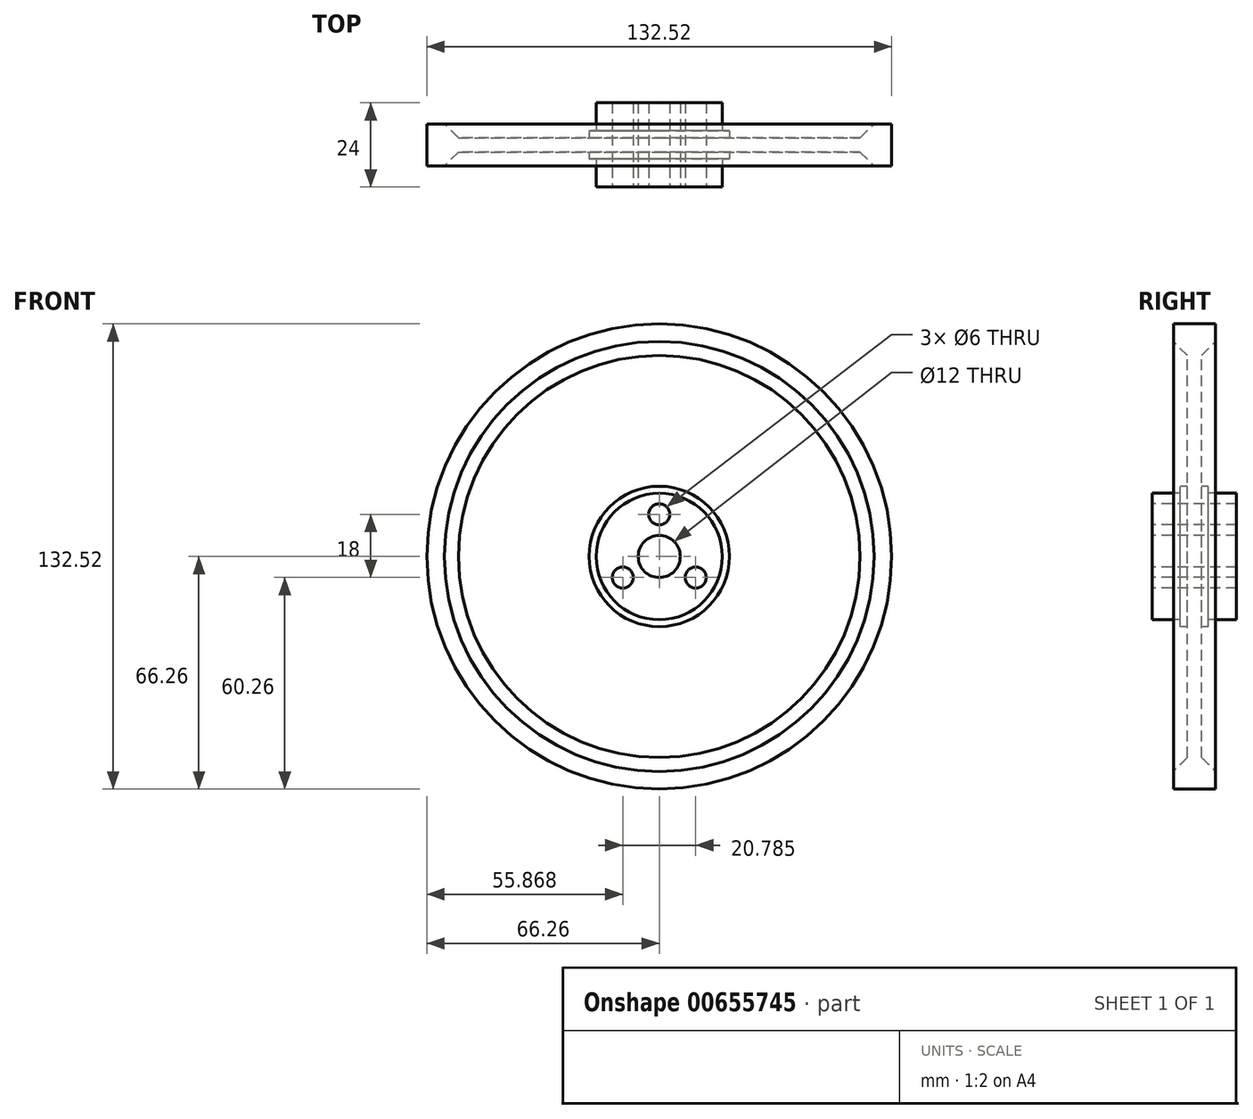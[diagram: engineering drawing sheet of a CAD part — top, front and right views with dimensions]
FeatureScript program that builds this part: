
annotation { "Feature Type Name" : "Feature", "Feature Type Description" : "" }
export const myFeature = defineFeature(function(context is Context, id is Id, definition is map)
    precondition{}
    {
        {
            var Q0;
            Q0=qCreatedBy(makeId("Right.planeOp"),FACE);
            var sketch = newSketch(context, id + "F0", { "sketchPlane" : qUnion([Q0])});
            skLineSegment(sketch, "E0", {"start": v(0, 66.25) * mm, "end": v(-6, 66.25) * mm});
            skLineSegment(sketch, "E1", {"start": v(-12, 18) * mm, "end": v(-12, 6) * mm});
            skLineSegment(sketch, "E2", {"start": v(-12, 6) * mm, "end": v(0, 6) * mm});
            skLineSegment(sketch, "E3", {"start": v(-80.76, 0) * mm, "end": v(80.56, 0) * mm, "construction": true});
            skLineSegment(sketch, "E4", {"start": v(-12, 12) * mm, "end": v(33.3, 12) * mm, "construction": true});
            skLineSegment(sketch, "E5", {"start": v(-12, 18) * mm, "end": v(-4, 18) * mm});
            skLineSegment(sketch, "E6", {"start": v(-4, 18) * mm, "end": v(-4, 20) * mm});
            skLineSegment(sketch, "E7", {"start": v(-4, 20) * mm, "end": v(-2, 20) * mm});
            skLineSegment(sketch, "E8", {"start": v(-6, 61.25) * mm, "end": v(-6, 66.25) * mm});
            skLineSegment(sketch, "E9", {"start": v(-6, 61.25) * mm, "end": v(-2, 57.26) * mm});
            skLineSegment(sketch, "E10", {"start": v(-2, 57.26) * mm, "end": v(-2, 20) * mm});
            skLineSegment(sketch, "E11", {"start": v(0, 66.25) * mm, "end": v(0, 6) * mm, "construction": true});
            skLineSegment(sketch, "E12.MirrorCS", {"start": v(0, 66.25) * mm, "end": v(6, 66.25) * mm});
            skLineSegment(sketch, "E13.MirrorCS", {"start": v(6, 61.25) * mm, "end": v(6, 66.25) * mm});
            skLineSegment(sketch, "E14.MirrorCS", {"start": v(6, 61.25) * mm, "end": v(2, 57.26) * mm});
            skLineSegment(sketch, "E15.MirrorCS", {"start": v(2, 57.26) * mm, "end": v(2, 20) * mm});
            skLineSegment(sketch, "E16.MirrorCS", {"start": v(4, 20) * mm, "end": v(2, 20) * mm});
            skLineSegment(sketch, "E17.MirrorCS", {"start": v(4, 18) * mm, "end": v(4, 20) * mm});
            skLineSegment(sketch, "E18.MirrorCS", {"start": v(12, 18) * mm, "end": v(4, 18) * mm});
            skLineSegment(sketch, "E19.MirrorCS", {"start": v(12, 18) * mm, "end": v(12, 6) * mm});
            skLineSegment(sketch, "E20.MirrorCS", {"start": v(12, 6) * mm, "end": v(0, 6) * mm});
            skSolve(sketch);
        }
        {
            var Q0;
            Q0 = qSketchRegion(id + "F0", true);
            var Q1;
            Q1=sQuery(id+"F0.wireOp",EDGE,"E3");
            revolve(context, id + "F1", {"entities" : qUnion([Q0]), "axis" : qUnion([Q1]), "revolveType" : RevolveType.FULL});
        }
        {
            var Q0;
            Q0=makeQuery(id+"F1.opRevolve","SWEPT_FACE",FACE,{"disambiguationData":[OSD([sQuery(id+"F0.wireOp",EDGE,"E1")])]});
            var sketch = newSketch(context, id + "F2", { "sketchPlane" : qUnion([Q0])});
            skPoint(sketch, "E21", {"position": v(0, 12) * mm});
            skPoint(sketch, "E22.1.0", {"position": v(-10.4, -6) * mm});
            skPoint(sketch, "E22.2.0", {"position": v(10.4, -6) * mm});
            skPoint(sketch, "E22.center", {"position": v(0, 0) * mm});
            skSolve(sketch);
        }
        {
            var Q0;
            Q0=sQuery(id+"F2.wireOp",VERTEX,"E21");
            var Q1;
            Q1=sQuery(id+"F2.wireOp",VERTEX,"E22.2.0");
            var Q2;
            Q2=sQuery(id+"F2.wireOp",VERTEX,"E22.1.0");
            var Q3;
            Q3=makeQuery(id+"F1.opRevolve","SWEPT_BODY",BODY,{"disambiguationData":[OSD([sQuery(id+"F0.wireOp",EDGE,"E0"),sQuery(id+"F0.wireOp",EDGE,"E1"),sQuery(id+"F0.wireOp",EDGE,"E2"),sQuery(id+"F0.wireOp",EDGE,"E5"),sQuery(id+"F0.wireOp",EDGE,"E6"),sQuery(id+"F0.wireOp",EDGE,"E7"),sQuery(id+"F0.wireOp",EDGE,"E8"),sQuery(id+"F0.wireOp",EDGE,"E9"),sQuery(id+"F0.wireOp",EDGE,"E10"),sQuery(id+"F0.wireOp",EDGE,"E12.MirrorCS"),sQuery(id+"F0.wireOp",EDGE,"E13.MirrorCS"),sQuery(id+"F0.wireOp",EDGE,"E14.MirrorCS"),sQuery(id+"F0.wireOp",EDGE,"E15.MirrorCS"),sQuery(id+"F0.wireOp",EDGE,"E16.MirrorCS"),sQuery(id+"F0.wireOp",EDGE,"E17.MirrorCS"),sQuery(id+"F0.wireOp",EDGE,"E18.MirrorCS"),sQuery(id+"F0.wireOp",EDGE,"E19.MirrorCS"),sQuery(id+"F0.wireOp",EDGE,"E20.MirrorCS")])]});
            hole(context, id + "F3", {"style" : HoleStyle.SIMPLE, "endStyle" : HoleEndStyle.THROUGH, "holeDiameter" : 6 * mm, "majorDiameter" : 5 * mm, "isTappedThrough" : true, "tappedDepth" : 12 * mm, "tapClearance" : 3, "locations" : qUnion([Q0, Q1, Q2]), "scope" : qUnion([Q3])});
        }
    });
